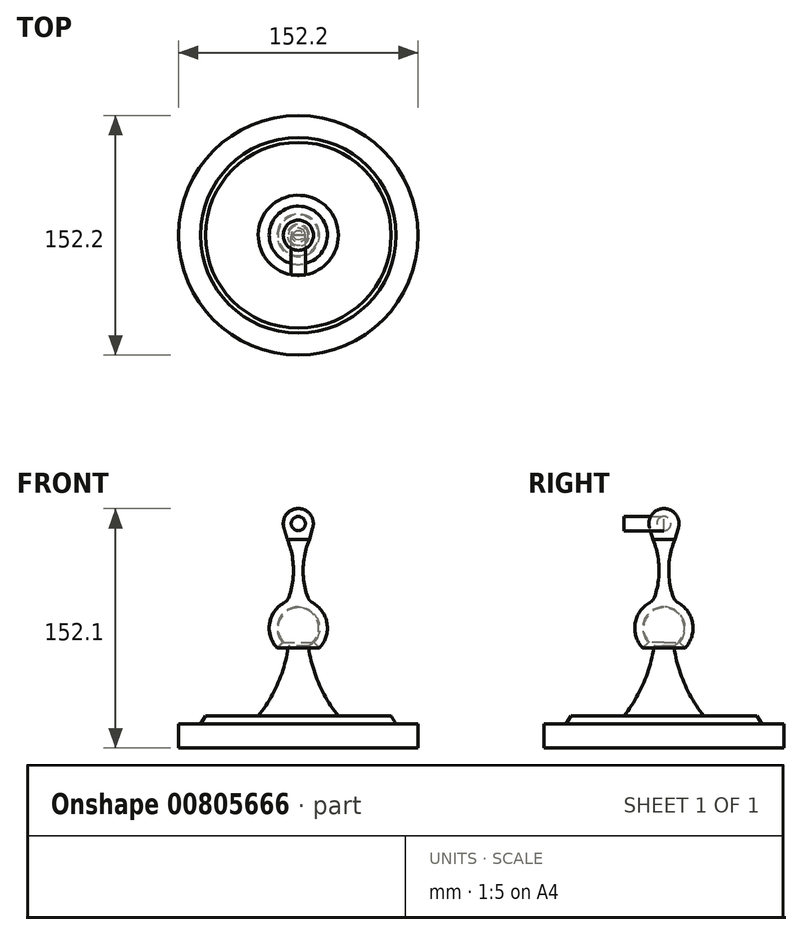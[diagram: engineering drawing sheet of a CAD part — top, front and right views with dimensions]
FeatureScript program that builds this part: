
annotation { "Feature Type Name" : "Feature", "Feature Type Description" : "" }
export const myFeature = defineFeature(function(context is Context, id is Id, definition is map)
    precondition{}
    {
        {
            var Q0;
            Q0=qCreatedBy(makeId("Front.planeOp"),FACE);
            var sketch = newSketch(context, id + "F0", { "sketchPlane" : qUnion([Q0])});
            skArc(sketch, "E0", {"start": v(0, 13.47) * mm, "mid": v(-12.35, 5.38) * mm, "end": v(-9.86, -9.18) * mm});
            skArc(sketch, "E1", {"start": v(-8.93, 16.18) * mm, "mid": v(-18.25, 2.92) * mm, "end": v(-13.53, -12.6) * mm});
            skLineSegment(sketch, "E2", {"start": v(-9.86, -9.18) * mm, "end": v(-13.53, -12.6) * mm});
            skLineSegment(sketch, "E3", {"start": v(0, 0) * mm, "end": v(0, 18.48) * mm});
            skLineSegment(sketch, "E4", {"start": v(0, 18.48) * mm, "end": v(0, 61.82) * mm});
            skArc(sketch, "E5", {"start": v(-6.01, 19.61) * mm, "mid": v(-3.09, 38.04) * mm, "end": v(-6.98, 56.29) * mm});
            skLineSegment(sketch, "E6", {"start": v(0, 56.77) * mm, "end": v(0, 61.82) * mm});
            skArc(sketch, "E7", {"start": v(0, 75.9) * mm, "mid": v(-7.67, 72.05) * mm, "end": v(-9.16, 63.6) * mm});
            skLineSegment(sketch, "E8", {"start": v(-6.98, 56.29) * mm, "end": v(-9.16, 63.6) * mm});
            skLineSegment(sketch, "E9.trimOffspring", {"start": v(0, 70.85) * mm, "end": v(0, 75.9) * mm});
            skPoint(sketch, "E10.MirrorCS.end.orphan", {"position": v(6.98, 56.29) * mm});
            skPoint(sketch, "E10.MirrorCS.start.orphan", {"position": v(6.98, 17.11) * mm});
            skPoint(sketch, "E11.MirrorCS.end.orphan", {"position": v(9.16, 63.6) * mm});
            skCircle(sketch, "E12", {"center": v(0, 66.33) * mm, "radius": 4.51 * mm});
            skPoint(sketch, "E13.newPointA", {"position": v(-6.98, 17.11) * mm});
            skArc(sketch, "E13.filletArc", {"start": v(-8.93, 16.18) * mm, "mid": v(-7.16, 17.63) * mm, "end": v(-6.01, 19.61) * mm});
            skSolve(sketch);
        }
        {
            var Q0;
            {var subQ5=sQuery(id+"F0.wireOp",EDGE,"E0");Q0=makeQuery(id+"F0.imprint","IMPRINT",FACE,{"disambiguationData":[TD([[makeQuery(id+"F0.imprint","IMPRINT",EDGE,{"derivedFrom":subQ5}),-1.0]])]});}
            var Q1;
            Q1=sQuery(id+"F0.wireOp",EDGE,"E3");
            revolve(context, id + "F1", {"surfaceOperationType" : NewSurfaceOperationType.NEW, "entities" : qUnion([Q0]), "axis" : qUnion([Q1]), "revolveType" : RevolveType.FULL});
        }
        {
            var Q0;
            {var subQ0=sQuery(id+"F0.wireOp",EDGE,"E12");var subQ1=makeQuery(id+"F0.imprint","INTERSECT",VERTEX,{"derivedFrom":[sQuery(id+"F0.wireOp",EDGE,"E6"),subQ0]});Q0=makeQuery(id+"F0.imprint","IMPRINT",FACE,{"disambiguationData":[TD([[makeQuery(id+"F0.imprint","IMPRINT",EDGE,{"disambiguationData":[TD([[subQ1,1.0]])],"derivedFrom":subQ0}),1.0]])]});}
            extrude(context, id + "F2", {"entities" : qUnion([Q0]), "depth" : 25.4 * mm, "offsetDistance" : 25.4 * mm});
        }
        {
            var Q0;
            Q0=qCreatedBy(makeId("Front.planeOp"),FACE);
            var sketch = newSketch(context, id + "F3", { "sketchPlane" : qUnion([Q0])});
            skArc(sketch, "E14", {"start": v(0, 12.95) * mm, "mid": v(-12.95, 0) * mm, "end": v(0, -12.95) * mm});
            skLineSegment(sketch, "E15", {"start": v(0, 0) * mm, "end": v(0, -76.2) * mm});
            skPoint(sketch, "E16.visualSharp", {"position": v(-23.94, -41.36) * mm});
            skPoint(sketch, "E17.visualSharp", {"position": v(-6.24, -28.7) * mm});
            skArc(sketch, "E18", {"start": v(-25.43, -55.89) * mm, "mid": v(-12.9, -34.88) * mm, "end": v(-6.24, -11.35) * mm});
            skLineSegment(sketch, "E19", {"start": v(0, -76.2) * mm, "end": v(-76.1, -76.2) * mm});
            skLineSegment(sketch, "E20", {"start": v(-76.1, -76.2) * mm, "end": v(-76.1, -60.92) * mm});
            skLineSegment(sketch, "E21", {"start": v(-76.1, -60.92) * mm, "end": v(-62.13, -60.92) * mm});
            skLineSegment(sketch, "E22", {"start": v(-25.43, -55.89) * mm, "end": v(-58.96, -55.89) * mm});
            skLineSegment(sketch, "E23", {"start": v(-58.96, -55.89) * mm, "end": v(-62.13, -60.92) * mm});
            skPoint(sketch, "E24.end.orphan", {"position": v(-62.13, -55.89) * mm});
            skLineSegment(sketch, "E25", {"start": v(0, 0) * mm, "end": v(0, 12.95) * mm});
            skSolve(sketch);
        }
        {
            var Q0;
            {var subQ0=sQuery(id+"F3.wireOp",EDGE,"E25");Q0=makeQuery(id+"F3.imprint","IMPRINT",FACE,{"disambiguationData":[TD([[makeQuery(id+"F3.imprint","IMPRINT",EDGE,{"derivedFrom":subQ0}),1.0]])]});}
            var Q1;
            Q1=sQuery(id+"F3.wireOp",EDGE,"E15");
            revolve(context, id + "F4", {"surfaceOperationType" : NewSurfaceOperationType.NEW, "entities" : qUnion([Q0]), "axis" : qUnion([Q1]), "revolveType" : RevolveType.FULL});
        }
        {
            var Q0;
            {var subQ1=sQuery(id+"F3.wireOp",EDGE,"E18");Q0=makeQuery(id+"F3.imprint","IMPRINT",FACE,{"disambiguationData":[TD([[makeQuery(id+"F3.imprint","IMPRINT",EDGE,{"derivedFrom":subQ1}),-1.0]])]});}
            var Q1;
            Q1=sQuery(id+"F3.wireOp",EDGE,"E15");
            revolve(context, id + "F5", {"operationType" : NewBodyOperationType.ADD, "surfaceOperationType" : NewSurfaceOperationType.NEW, "entities" : qUnion([Q0]), "axis" : qUnion([Q1]), "revolveType" : RevolveType.FULL});
        }
    });
